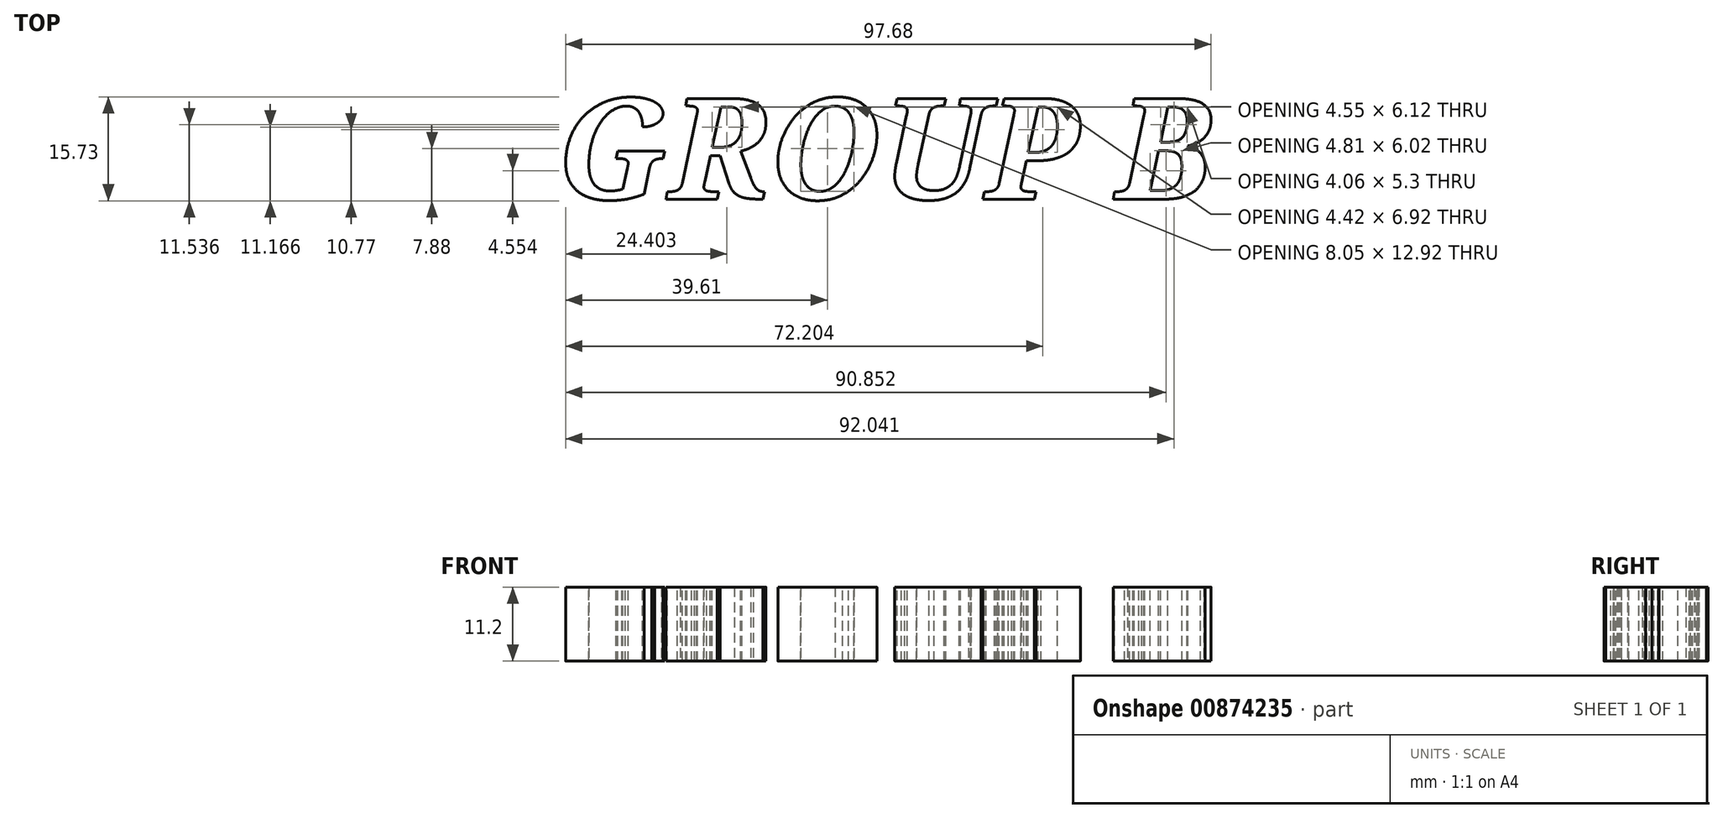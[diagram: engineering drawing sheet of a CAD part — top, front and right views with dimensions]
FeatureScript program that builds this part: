
annotation { "Feature Type Name" : "Feature", "Feature Type Description" : "" }
export const myFeature = defineFeature(function(context is Context, id is Id, definition is map)
    precondition{}
    {
        {
            var Q0;
            Q0=qCreatedBy(makeId("Top.planeOp"),FACE);
            var sketch = newSketch(context, id + "F0", { "sketchPlane" : qUnion([Q0])});
            skText(sketch, "E0", { "text": "GROUP B", "fontName": "NotoSerif-BoldItalic.ttf"});
            const initialGuessF0  = {"E0": [-0.0451, 0.00635, 1, 0, 0.01538]};
            skSetInitialGuess(sketch, initialGuessF0);
            skSolve(sketch);
        }
        {
            var Q0;
            Q0 = qSketchRegion(id + "F0", true);
            extrude(context, id + "F1", {"entities" : qUnion([Q0]), "oppositeDirection" : true, "depth" : 11.2 * mm, "offsetDistance" : 25 * mm});
        }
    });
